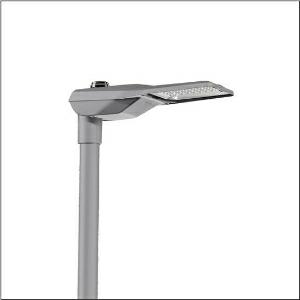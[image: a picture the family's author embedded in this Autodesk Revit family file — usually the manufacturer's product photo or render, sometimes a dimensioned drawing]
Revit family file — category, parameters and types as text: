
# Revit family: streetlight_sl_21_mini___st1_0a_5xe6d37n08hb_abde
name_source: partatom
category: Lighting Fixtures
units: mm (PartAtom-declared; Revit-internal decimal feet)

## family parameters
Cut with Voids When Loaded = No
Host = Face
Light Source = No
Part Type = Normal
Room Calculation Point = No
Round Connector Dimension = Use Diameter
Shared = No

## types (1)
- --- (1 x LED, 9040 lm, 66 W, 3000K)
    Apparent Load = 66 VA
    CIE Flux Codes = 37 72 97 100 100
    Color Rendering = 70
    Color Temperature = 3000K
    Default Elevation = 1800 mm
    Description = Streetlight SL 21 mini, mast luminaire, primary light control with lens, of PMMA, primary optical cover: cover, of toughened safety glass, transparent, light distribution: ST1.0a, light emission: direct distribution, primary light characteristic: asymmetric, installation type: side-entry, LED, 3G 1.5mm², High Power LED, rated luminous flux: 9.040lm, luminous efficacy: 137lm/W, light colour: 730, colour temperature: 3000K, control gear: NEMA (7pin), control: overheat protection, pre-setting: linear dimming characteristic, constant luminous flux control, time-dependent luminous flux control, flexible luminous flux parameterisation, mains connection: 230..240V, AC, 50/60Hz, connection cable pre-assembled, cable length: 8,5m, wiring characteristics: H07RN-F, start of lifetime: 66W, end of service life: 69W, reduction: 30W, luminaire housing, of diecast aluminium (EN AC-44300), powder-coated, SITECO metallic grey (DB 702S), corrosivity category C5 high according to DIN EN ISO 12944, multi-level sealing system, sealing non-destructively replaceable, inclination adjustable: 0°, 5°, 10°, 15°, length: 628mm, width: 235mm, height: 110mm, spigot size: 42mm (side-entry), mounting height: 4..8m, protection rating (complete): IP66, insulation class (complete): insulation class I (protective earthing), certification: CE, ENEC, ENEC+, VDE, impact resistance: IK10, permissible operating ambient temperature for outdoor applications: -40..+50°C, standard-compliant lighting for roads and squares, packaging unit: 1 piece

Light Distribution: ST1.0a
    Height = 110 mm
    Lamp = 1 x LED
    Lamp Light Flux = 9040 lm
    Lamp Power = 66 W
    Lamp count = 1
    Length = 625 mm
    Luminous efficacy = 137 lm/W
    Manufacturer = Siteco
    ModVariant = No
    Model = 5XE6D37N08HB
    Number of Poles = 1
    OnlyDefault = Yes
    Power Factor = 1
    Product Name = Streetlight SL 21 mini | ST1.0a
    Product group = mast luminaire | pylon top
    ProductGroupID = 6100
    Protection Class = Protection class I
    Protection Degree = IP 66
    RLX_Detail_Level = 1
    RLX_Emergency_Light_Flux = 0 lm
    RLX_Emergency_Type = 0
    RLX_Emergency_Type_DB = No
    RlxData = <blob elided: 26193 chars, md5=7d9e265d>
    Socket = socket
    Standby Power = 0 W
    System Light Flux = 9040 lm
    System Power = 66 W
    Type Comments = factory setting: luminous flux: 100 % | dim-lin: 254 | 670 mA
    Type Image = l_1294379.jpg
    URL = http://relux.com
    VarID = @adj_135777
    Voltage = 0 V
    Weight = 0.00 kg
    Width = 234 mm

## geometry (parser evidence)
native form markers: Blend x4, Sweep x11
no freeform markers — native parametric forms only
